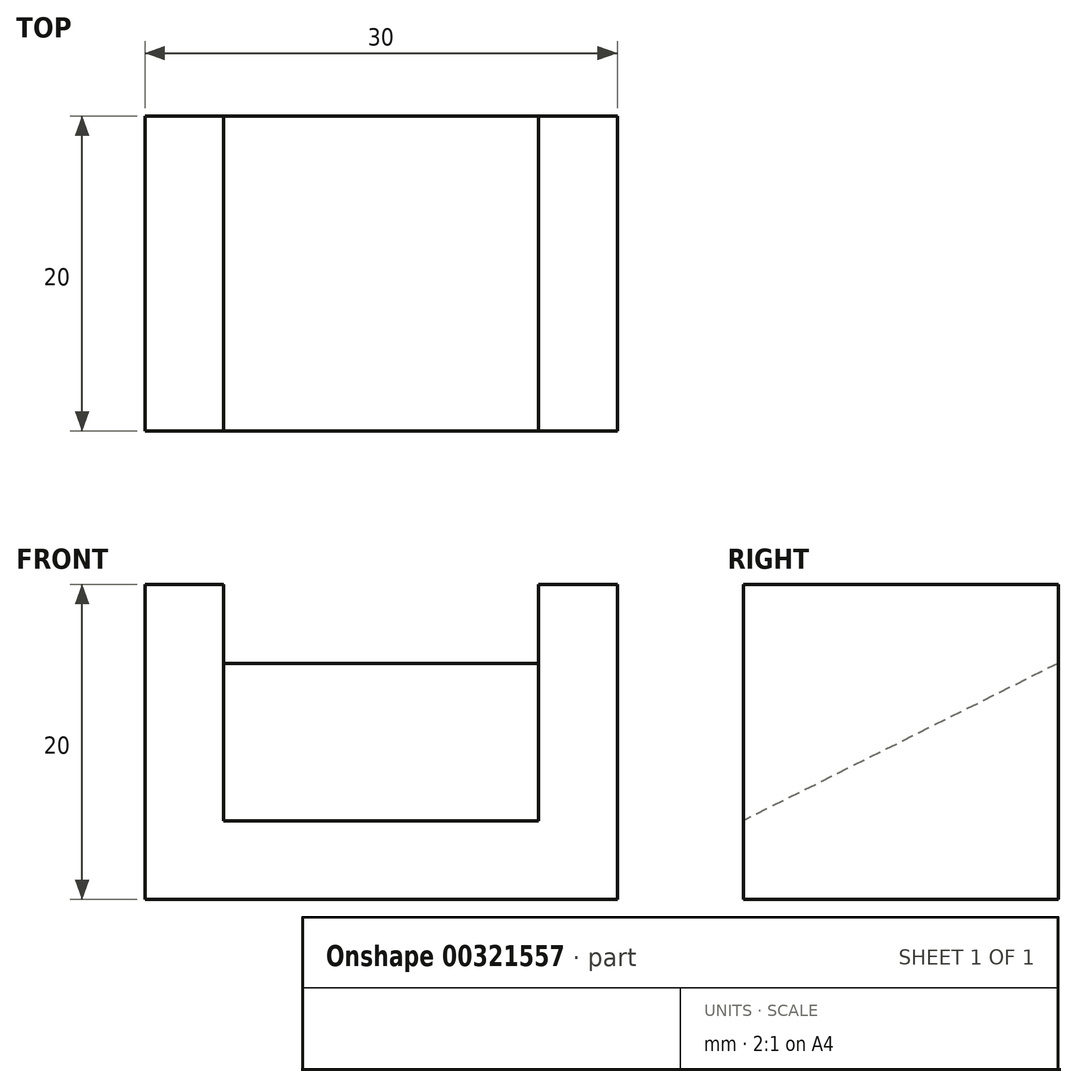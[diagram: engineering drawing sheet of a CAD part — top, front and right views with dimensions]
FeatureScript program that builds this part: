
annotation { "Feature Type Name" : "Feature", "Feature Type Description" : "" }
export const myFeature = defineFeature(function(context is Context, id is Id, definition is map)
    precondition{}
    {
        {
            var Q0;
            Q0=qCreatedBy(makeId("Front.planeOp"),FACE);
            var sketch = newSketch(context, id + "F0", { "sketchPlane" : qUnion([Q0])});
            skLineSegment(sketch, "E0", {"start": v(-15, 0) * mm, "end": v(-15, 20) * mm});
            skLineSegment(sketch, "E1", {"start": v(-15, 20) * mm, "end": v(15, 20) * mm});
            skLineSegment(sketch, "E2", {"start": v(15, 20) * mm, "end": v(15, 0) * mm});
            skLineSegment(sketch, "E3", {"start": v(15, 0) * mm, "end": v(-15, 0) * mm});
            skSolve(sketch);
        }
        {
            var Q0;
            Q0 = qSketchRegion(id + "F0", true);
            extrude(context, id + "F1", {"entities" : qUnion([Q0]), "depth" : 20 * mm});
        }
        {
            var Q0;
            Q0=qCreatedBy(makeId("Right.planeOp"),FACE);
            var sketch = newSketch(context, id + "F2", { "sketchPlane" : qUnion([Q0])});
            skLineSegment(sketch, "E4", {"start": v(0, 15) * mm, "end": v(-20, 5) * mm});
            skLineSegment(sketch, "E5", {"start": v(-20, 5) * mm, "end": v(-20, 15) * mm});
            skLineSegment(sketch, "E6", {"start": v(-20, 15) * mm, "end": v(0, 15) * mm});
            skLineSegment(sketch, "E7", {"start": v(0, 15) * mm, "end": v(0, 20) * mm});
            skLineSegment(sketch, "E8", {"start": v(0, 20) * mm, "end": v(-20, 20) * mm});
            skLineSegment(sketch, "E9", {"start": v(-20, 20) * mm, "end": v(-20, 15) * mm});
            skSolve(sketch);
        }
        {
            var Q0;
            Q0 = qSketchRegion(id + "F2", true);
            extrude(context, id + "F3", {"entities" : qUnion([Q0]), "operationType" : NewBodyOperationType.REMOVE, "oppositeDirection" : true, "depth" : 10 * mm, "hasSecondDirection" : true, "secondDirectionOppositeDirection" : false, "secondDirectionDepth" : 10 * mm});
        }
    });
